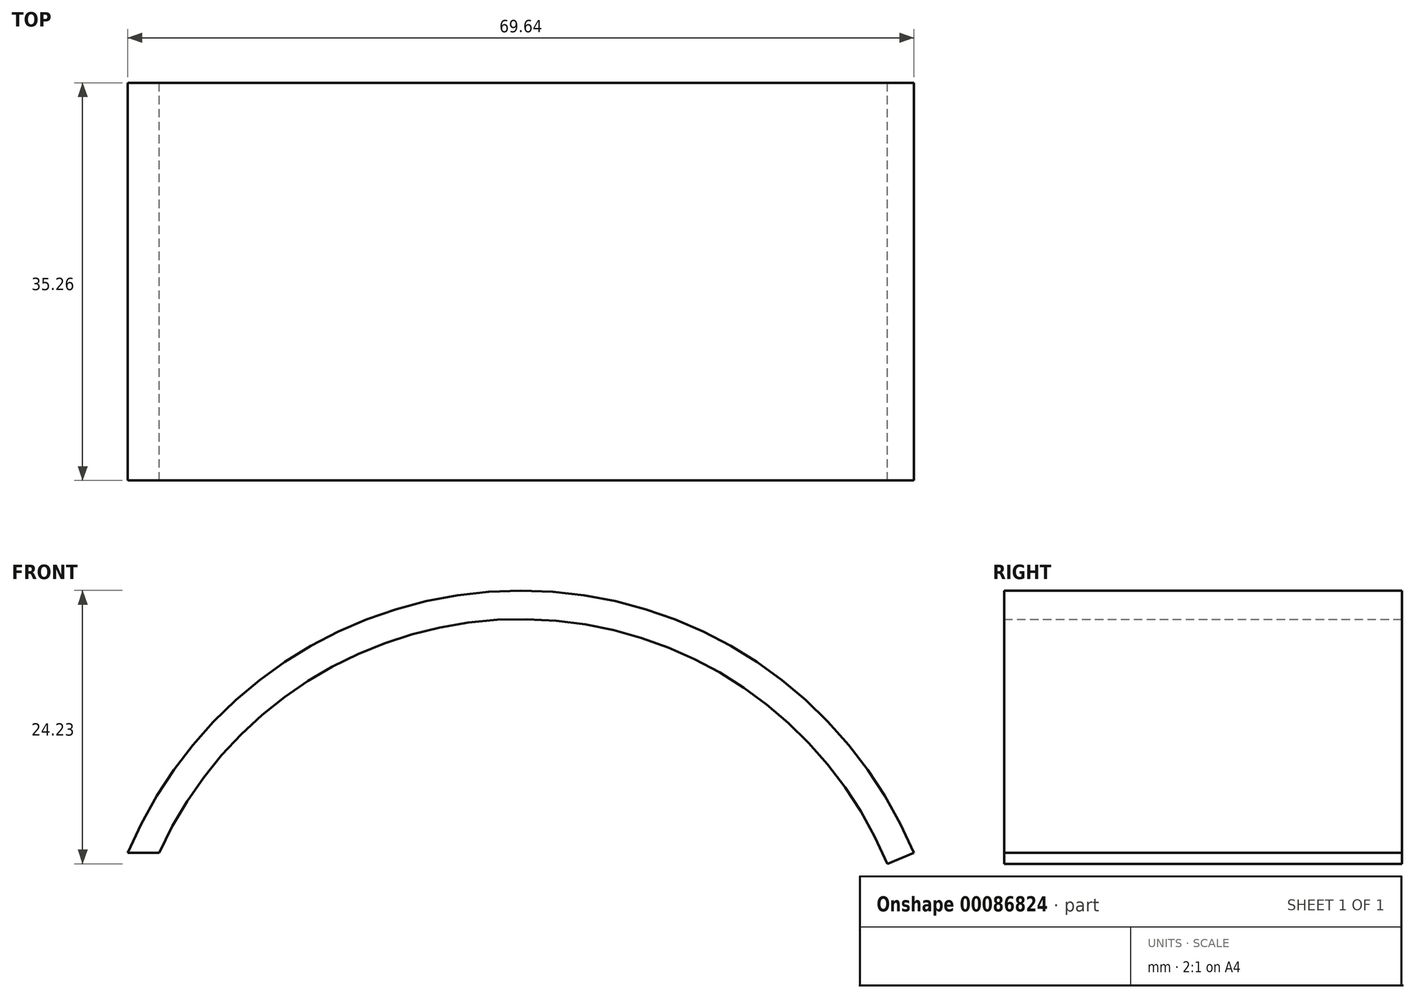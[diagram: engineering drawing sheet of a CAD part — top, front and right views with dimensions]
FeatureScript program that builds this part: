
annotation { "Feature Type Name" : "Feature", "Feature Type Description" : "" }
export const myFeature = defineFeature(function(context is Context, id is Id, definition is map)
    precondition{}
    {
        {
            var Q0;
            Q0=qCreatedBy(makeId("Front.planeOp"),FACE);
            var sketch = newSketch(context, id + "F0", { "sketchPlane" : qUnion([Q0])});
            skArc(sketch, "E0", {"start": v(34.82, 0) * mm, "mid": v(0, 23.26) * mm, "end": v(-34.82, 0) * mm});
            skArc(sketch, "E1.0", {"start": v(32.47, -0.97) * mm, "mid": v(0, 20.72) * mm, "end": v(-32.47, -0.97) * mm});
            skLineSegment(sketch, "E2", {"start": v(-34.82, 0) * mm, "end": v(-32.05, 0) * mm});
            skLineSegment(sketch, "E3", {"start": v(34.82, 0) * mm, "end": v(32.47, -0.97) * mm});
            skSolve(sketch);
        }
        {
            var Q0;
            Q0 = qSketchRegion(id + "F0", true);
            extrude(context, id + "F1", {"entities" : qUnion([Q0]), "depth" : 35.26 * mm});
        }
    });
